# Revit family: Lavatory_System-Wall_Mount-Trueform_Concrete-Single_Ramp_Basin-Configurable_3_or_4_Station
name_source: partatom
category: Plumbing Fixtures
revit_build: Autodesk Revit LT 2015 (Build: 20140606_1530(x64)
units: mm (PartAtom-declared; Revit-internal decimal feet)

## types (3) — shared parameters
ABAC = 18"
ABC = Yes
AHC = 5"
Additional Support Required Note = No
Apron Height = 5"
Apron Height MIN = 5"
BDC = 19"
BSC = 3"
Basin Depth = 12"
Basin Front Setback = 3"
Basin Front Setback MAX = 7"
Basin Height = 5"
Basin/Countertop Reconciliation Warning = No
Bracket Placement Warning = No
Brackets = Steel, Paint Finish, Dark Gray, Matte
LAB2C = No
Lavatory = GFRC - Concrete
Left Bracket Placement MAX = 4 1/2"
Left Bracket Placement MIN = 1 1/2"
Left T Bracket Placement from Countertop Edge = 3"
Manufacturer = Trueform Concrete
Non Standard Sink Basin Model Note = No
ODC = 21"
Overall Countertop Depth = 21"
Overall Countertop Depth MAX = 24"
Overall Countertop Depth MIN = 17"
RAB2C = No
RLAC = 1/8"
RRAC = 1/8"
Remove Left Apron = No
Remove Right Apron = No
Right Bracket Placement MAX = 4 1/2"
Right Bracket Placement MIN = 1 1/2"
Right T Bracket Placement from Countertop Edge = 3"
Substrate = Plywood, Sheathing
Tailpiece = Polished Chrome
URL = https://www.trueformconcrete.com
Use Adjustable Brackets = Yes
Use Left T Bracket = Yes
Use Right T Bracket = Yes
Vent Connection = No
Verify Basin Front Setback = 3"
Verify Left Bracket Placement = 3"
Verify Overall Countertop Depth = 21"
Verify Rear Countertop = 6"
Verify Right Bracket Placement = 3"
WFU = 6
Waste Connection = Yes
Waste Fitting = 1 1/2"

## per-type parameters (varying)
| type | Basin Center to Countertop Edge MAX | Basin Center to Countertop Edge MIN | Basin Center to Left Countertop Edge | Basin Center to Right Countertop Edge | Basin ID (Do not edit value) | Basin Length | CWFU | Description | HWFU | LAB1C | LCC | Overall Countertop Length | Overall Countertop Length MIN | RAB1C | RCC | SDC | Verify Basin Center to Left Countertop Edge | Verify Basin Center to Right Countertop Edge | Verify Overall Countertop Length |
| R-9612 | 57" | 51" | 54" | 54" | 9612 | 96" | 1.5 | Wall-mount GFRC 3 or 4 Station Single Ramp Basin Lavatory | 1.5 | 28" | 54" | 108" | 102" | 28" | 54" | 5/8" | 54" | 54" | 108" |
| R-11012 | 64" | 58" | 61" | 61" | 11012 | 110" | 2 | Wall-mount GFRC 4 Station Single Ramp Basin Lavatory | 2 | 31 1/2" | 61" | 122" | 116" | 31 1/2" | 61" | 3/4" | 61" | 61" | 122" |
| R-8012 | 49" | 43" | 46" | 46" | 8012 | 80" | 1.5 | Wall-mount GFRC 3 Station Single Ramp Basin Lavatory | 1.5 | 24" | 46" | 92" | 86" | 24" | 46" | 1/2" | 46" | 46" | 92" |

note: column(s) folded — value = type name in every type: Model

## geometry (parser evidence)
native form markers: Sweep x6
no freeform markers — native parametric forms only
